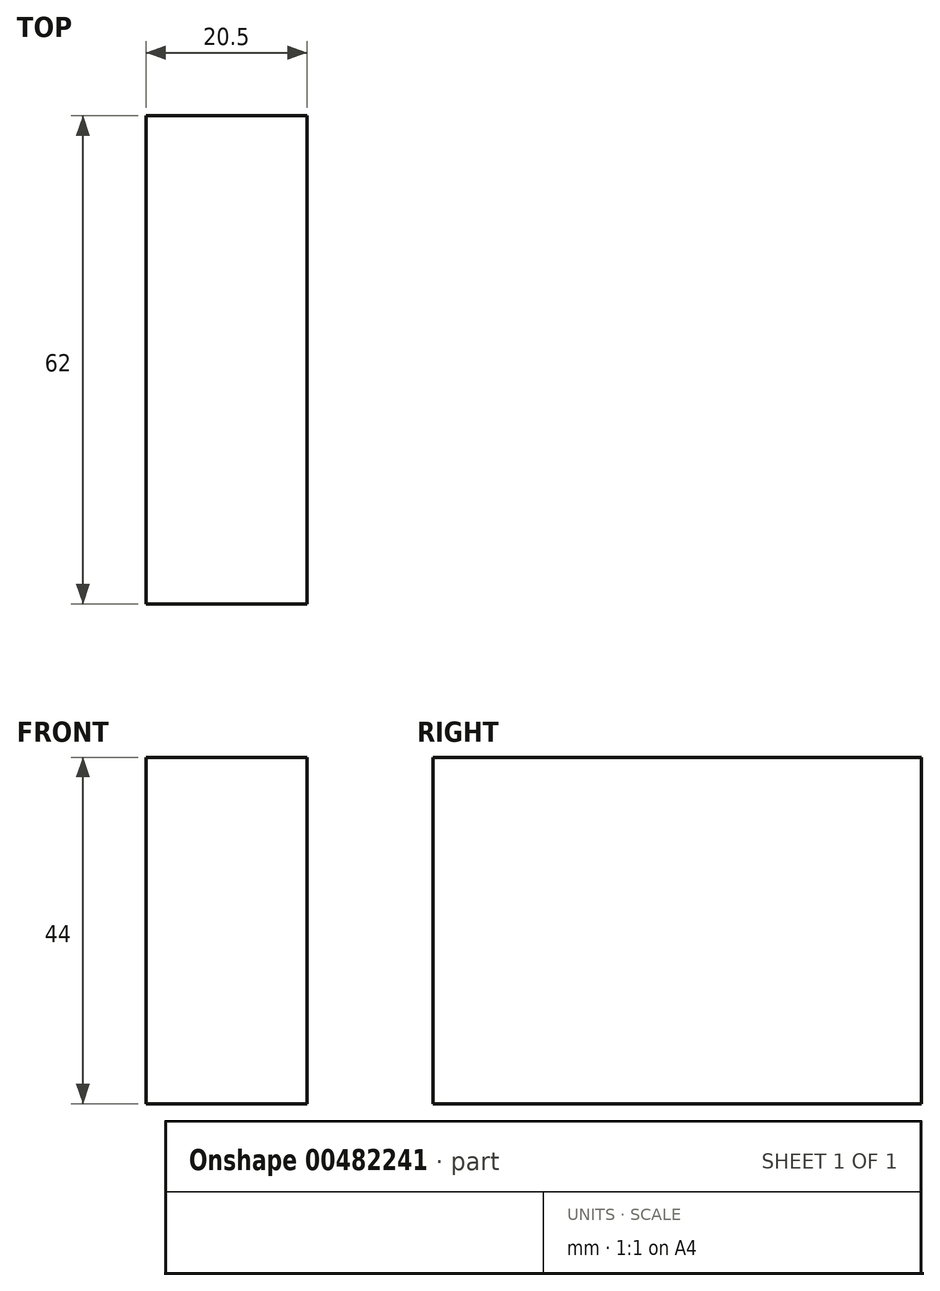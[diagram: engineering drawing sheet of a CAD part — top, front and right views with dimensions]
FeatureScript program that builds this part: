
annotation { "Feature Type Name" : "Feature", "Feature Type Description" : "" }
export const myFeature = defineFeature(function(context is Context, id is Id, definition is map)
    precondition{}
    {
        {
            var Q0;
            Q0=qCreatedBy(makeId("Front.planeOp"),FACE);
            var sketch = newSketch(context, id + "F0", { "sketchPlane" : qUnion([Q0])});
            skLineSegment(sketch, "E0.bottom", {"start": v(-10.25, 22) * mm, "end": v(10.25, 22) * mm});
            skLineSegment(sketch, "E0.top", {"start": v(-10.25, -22) * mm, "end": v(10.25, -22) * mm});
            skLineSegment(sketch, "E0.left", {"start": v(-10.25, 22) * mm, "end": v(-10.25, -22) * mm});
            skLineSegment(sketch, "E0.right", {"start": v(10.25, 22) * mm, "end": v(10.25, -22) * mm});
            skPoint(sketch, "E0.middle", {"position": v(0, 0) * mm});
            skSolve(sketch);
        }
        {
            var Q0;
            Q0 = qSketchRegion(id + "F0", true);
            extrude(context, id + "F1", {"entities" : qUnion([Q0]), "depth" : 62 * mm});
        }
    });
